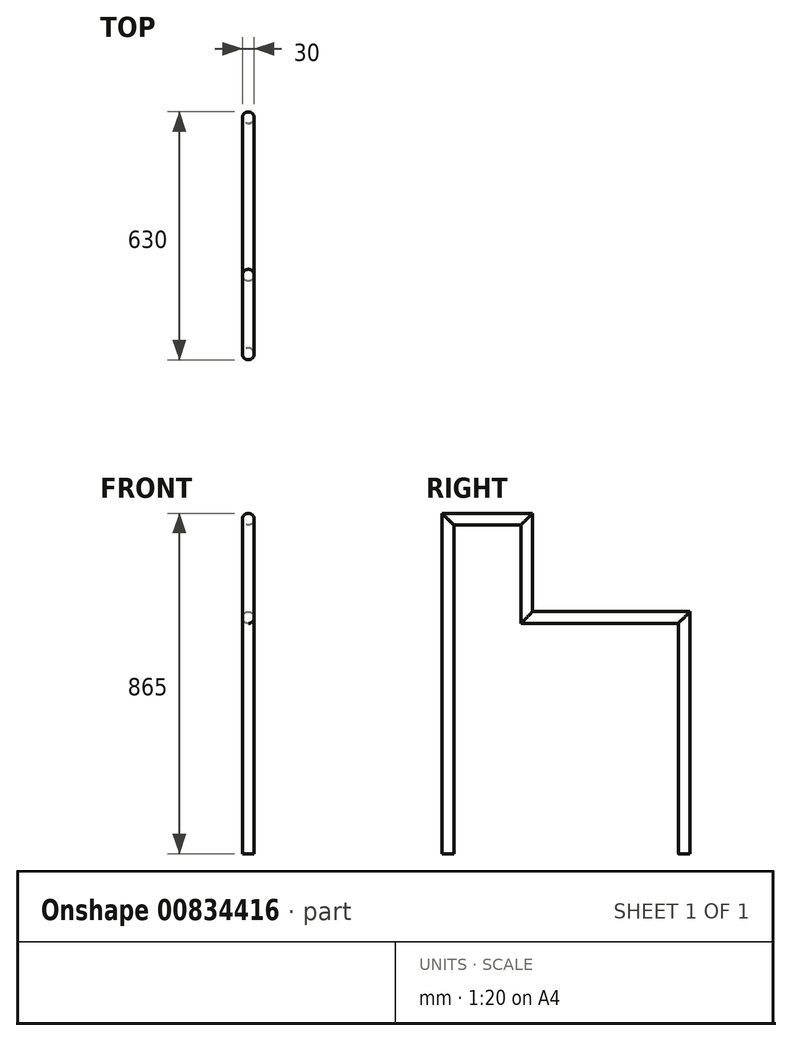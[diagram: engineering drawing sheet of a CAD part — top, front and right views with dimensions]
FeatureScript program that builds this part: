
annotation { "Feature Type Name" : "Feature", "Feature Type Description" : "" }
export const myFeature = defineFeature(function(context is Context, id is Id, definition is map)
    precondition{}
    {
        {
            var Q0;
            Q0=qCreatedBy(makeId("Right.planeOp"),FACE);
            var sketch = newSketch(context, id + "F0", { "sketchPlane" : qUnion([Q0])});
            skLineSegment(sketch, "E0", {"start": v(0, 0) * mm, "end": v(0, 850) * mm});
            skLineSegment(sketch, "E1", {"start": v(0, 850) * mm, "end": v(200, 850) * mm});
            skLineSegment(sketch, "E2", {"start": v(200, 850) * mm, "end": v(200, 600) * mm});
            skLineSegment(sketch, "E3", {"start": v(200, 600) * mm, "end": v(600, 600) * mm});
            skLineSegment(sketch, "E4", {"start": v(600, 600) * mm, "end": v(600, 0) * mm});
            skSolve(sketch);
        }
        {
            var Q0;
            Q0=qCreatedBy(makeId("Top.planeOp"),FACE);
            var sketch = newSketch(context, id + "F1", { "sketchPlane" : qUnion([Q0])});
            skCircle(sketch, "E5", {"center": v(0, 0) * mm, "radius": 15 * mm});
            skSolve(sketch);
        }
        {
            var Q0;
            Q0 = qSketchRegion(id + "F1", true);
            var Q1;
            Q1 = qConstructionFilter(qBodyType(qCreatedBy(id + "F0" ,EDGE), BodyType.WIRE), ConstructionObject.NO);
            sweep(context, id + "F2", {"profiles" : qUnion([Q0]), "path" : qUnion([Q1])});
        }
    });
